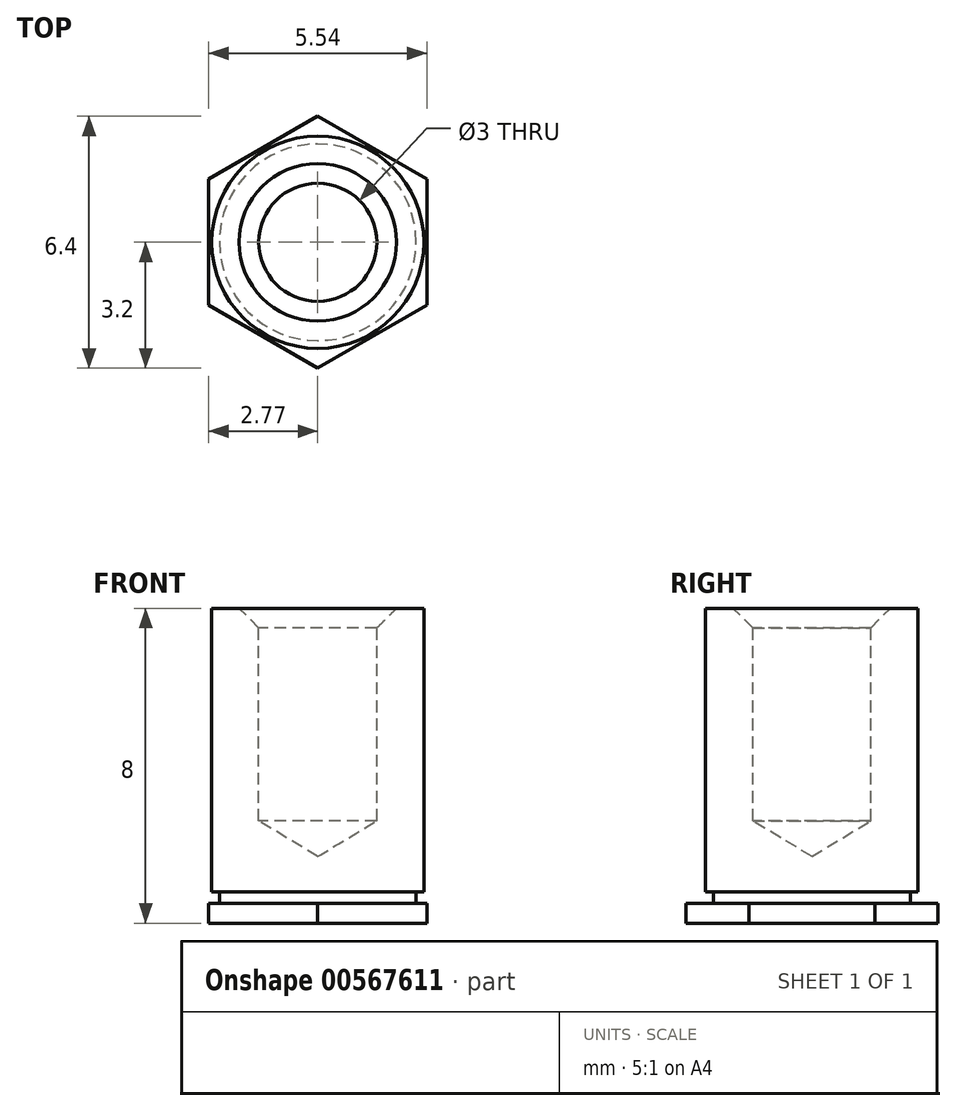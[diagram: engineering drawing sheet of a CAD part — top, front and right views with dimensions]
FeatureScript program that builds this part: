
annotation { "Feature Type Name" : "Feature", "Feature Type Description" : "" }
export const myFeature = defineFeature(function(context is Context, id is Id, definition is map)
    precondition{}
    {
        {
            var Q0;
            Q0=qCreatedBy(makeId("Top.planeOp"),FACE);
            var sketch = newSketch(context, id + "F0", { "sketchPlane" : qUnion([Q0])});
            skCircle(sketch, "E0.cCircle", {"center": v(0, 0) * mm, "radius": 3.2 * mm, "construction": true});
            skLineSegment(sketch, "E0.0", {"start": v(0, -3.2) * mm, "end": v(-2.77, -1.6) * mm});
            skLineSegment(sketch, "E0.1", {"start": v(-2.77, -1.6) * mm, "end": v(-2.77, 1.6) * mm});
            skLineSegment(sketch, "E0.2", {"start": v(-2.77, 1.6) * mm, "end": v(0, 3.2) * mm});
            skLineSegment(sketch, "E0.3", {"start": v(0, 3.2) * mm, "end": v(2.77, 1.6) * mm});
            skLineSegment(sketch, "E0.4", {"start": v(2.77, 1.6) * mm, "end": v(2.77, -1.6) * mm});
            skLineSegment(sketch, "E0.5", {"start": v(2.77, -1.6) * mm, "end": v(0, -3.2) * mm});
            skSolve(sketch);
        }
        {
            var Q0;
            Q0 = qSketchRegion(id + "F0", true);
            extrude(context, id + "F1", {"entities" : qUnion([Q0]), "depth" : 0.5 * mm, "offsetDistance" : 25 * mm});
        }
        {
            var Q0;
            Q0=makeQuery(id+"F1.opExtrude","CAP_FACE",FACE,{"disambiguationData":[OSD([sQuery(id+"F0.wireOp",EDGE,"E0.0"),sQuery(id+"F0.wireOp",EDGE,"E0.1"),sQuery(id+"F0.wireOp",EDGE,"E0.2"),sQuery(id+"F0.wireOp",EDGE,"E0.3"),sQuery(id+"F0.wireOp",EDGE,"E0.4"),sQuery(id+"F0.wireOp",EDGE,"E0.5")])],"isStart":false});
            var sketch = newSketch(context, id + "F2", { "sketchPlane" : qUnion([Q0])});
            skCircle(sketch, "E1", {"center": v(0, 0) * mm, "radius": 2.5 * mm});
            skSolve(sketch);
        }
        {
            var Q0;
            Q0 = qSketchRegion(id + "F2", true);
            extrude(context, id + "F3", {"entities" : qUnion([Q0]), "operationType" : NewBodyOperationType.ADD, "depth" : 0.3 * mm, "offsetDistance" : 25 * mm});
        }
        {
            var Q0;
            Q0=makeQuery(id+"F3.opExtrude","CAP_FACE",FACE,{"disambiguationData":[OSD([sQuery(id+"F2.wireOp",EDGE,"E1")])],"isStart":false});
            var sketch = newSketch(context, id + "F4", { "sketchPlane" : qUnion([Q0])});
            skCircle(sketch, "E2", {"center": v(0, 0) * mm, "radius": 2.7 * mm});
            skSolve(sketch);
        }
        {
            var Q0;
            Q0 = qSketchRegion(id + "F4", true);
            extrude(context, id + "F5", {"entities" : qUnion([Q0]), "operationType" : NewBodyOperationType.ADD, "depth" : (6.8 + 0.4) * mm, "offsetDistance" : 25 * mm});
        }
        {
            var Q0;
            Q0=makeQuery(id+"F5.opExtrude","CAP_FACE",FACE,{"disambiguationData":[OSD([sQuery(id+"F4.wireOp",EDGE,"E2")])],"isStart":false});
            var sketch = newSketch(context, id + "F6", { "sketchPlane" : qUnion([Q0])});
            skCircle(sketch, "E3.0", {"center": v(0, 0) * mm, "radius": 2.7 * mm});
            skSolve(sketch);
        }
        {
            var Q0;
            Q0=sQuery(id+"F6.wireOp",VERTEX,"E3.0.center");
            var Q1;
            Q1=makeQuery(id+"F1.opExtrude","SWEPT_BODY",BODY,{"disambiguationData":[OSD([sQuery(id+"F0.wireOp",EDGE,"E0.0"),sQuery(id+"F0.wireOp",EDGE,"E0.1"),sQuery(id+"F0.wireOp",EDGE,"E0.2"),sQuery(id+"F0.wireOp",EDGE,"E0.3"),sQuery(id+"F0.wireOp",EDGE,"E0.4"),sQuery(id+"F0.wireOp",EDGE,"E0.5")])]});
            hole(context, id + "F7", {"style" : HoleStyle.C_SINK, "endStyle" : HoleEndStyle.BLIND, "holeDiameter" : 3 * mm, "cSinkDiameter" : 4 * mm, "cSinkAngle" : 90 * degree, "holeDepth" : 5.4 * mm, "isTappedThrough" : true, "tappedDepth" : 12 * mm, "tapClearance" : 3, "locations" : qUnion([Q0]), "scope" : qUnion([Q1])});
        }
    });
